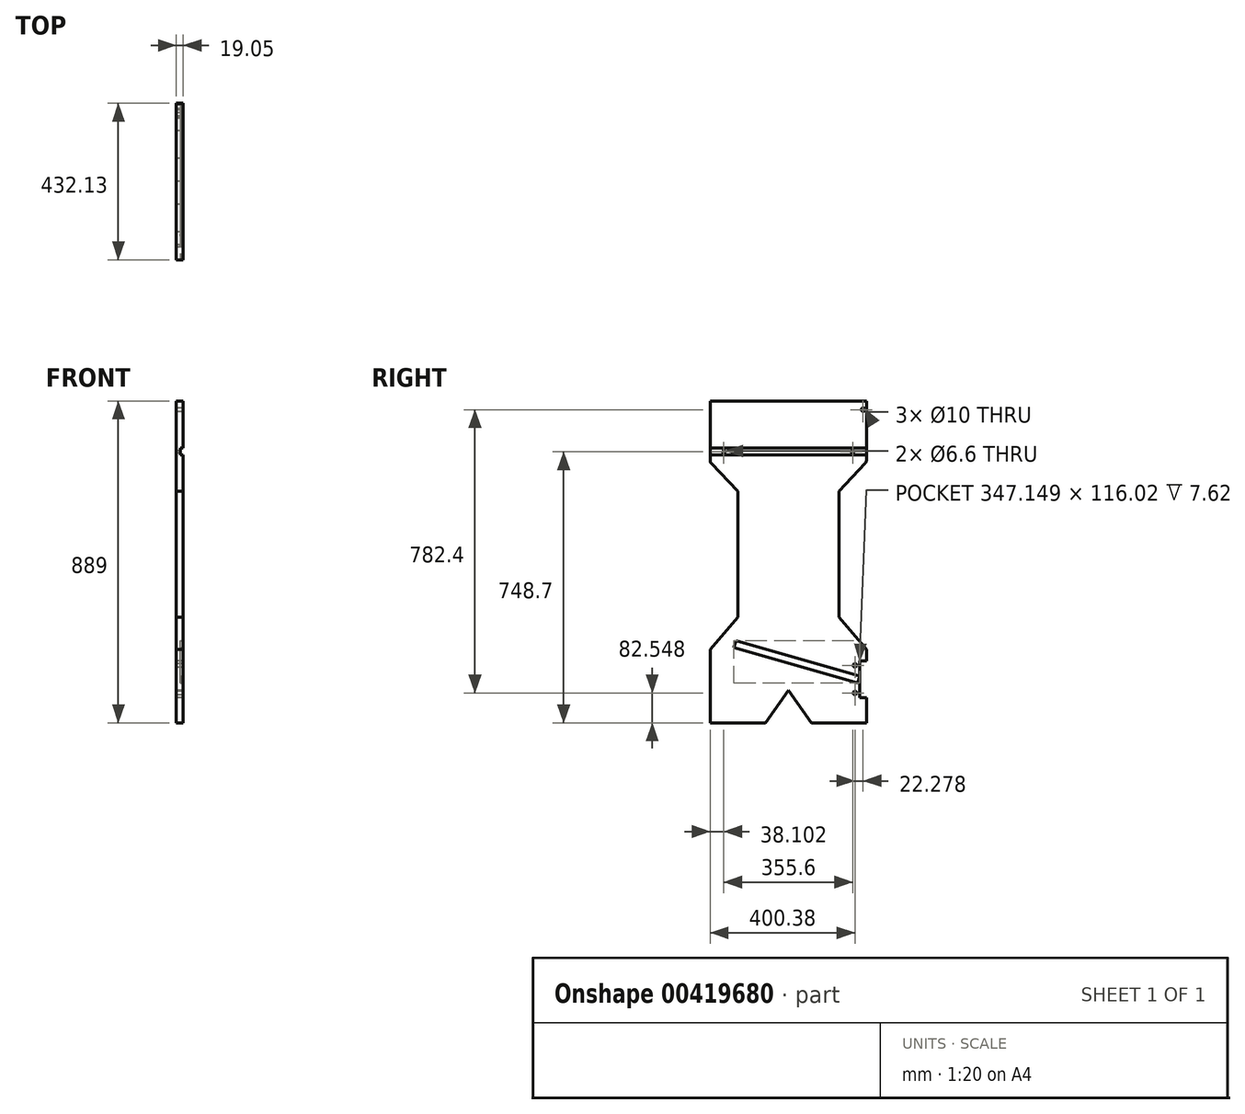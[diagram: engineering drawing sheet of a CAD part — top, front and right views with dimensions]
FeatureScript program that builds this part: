
annotation { "Feature Type Name" : "Feature", "Feature Type Description" : "" }
export const myFeature = defineFeature(function(context is Context, id is Id, definition is map)
    precondition{}
    {
        {
            var Q0;
            Q0=qCreatedBy(makeId("Right.planeOp"),FACE);
            var sketch = newSketch(context, id + "F0", { "sketchPlane" : qUnion([Q0])});
            skLineSegment(sketch, "E0.bottom", {"start": v(215.57, 77.66) * mm, "end": v(-216.23, 77.66) * mm});
            skLineSegment(sketch, "E0.left", {"start": v(215.57, 77.66) * mm, "end": v(215.57, -87.25) * mm});
            skLineSegment(sketch, "E0.right", {"start": v(-216.23, 77.66) * mm, "end": v(-216.23, -87.25) * mm});
            skPoint(sketch, "E0.middle", {"position": v(0, 0) * mm});
            skLineSegment(sketch, "E1", {"start": v(-213.4, -94.27) * mm, "end": v(-139.7, -171.26) * mm});
            skLineSegment(sketch, "E2", {"start": v(212.78, -94.24) * mm, "end": v(139.7, -171.26) * mm});
            skLineSegment(sketch, "E3", {"start": v(-139.7, -171.26) * mm, "end": v(-139.7, -519.24) * mm});
            skArc(sketch, "E4.filletArc", {"start": v(-216.23, -87.25) * mm, "mid": v(-215.5, -91.03) * mm, "end": v(-213.4, -94.27) * mm});
            skArc(sketch, "E5.filletArc", {"start": v(212.78, -94.24) * mm, "mid": v(214.85, -91.01) * mm, "end": v(215.57, -87.25) * mm});
            skLineSegment(sketch, "E6", {"start": v(-139.7, -519.24) * mm, "end": v(-215.9, -608.14) * mm});
            skLineSegment(sketch, "E7", {"start": v(-215.9, -608.14) * mm, "end": v(-215.9, -811.34) * mm});
            skLineSegment(sketch, "E8.MirrorCS", {"start": v(139.7, -171.26) * mm, "end": v(139.7, -519.24) * mm});
            skLineSegment(sketch, "E9.MirrorCS", {"start": v(139.7, -519.24) * mm, "end": v(215.9, -608.14) * mm});
            skLineSegment(sketch, "E10", {"start": v(-139.7, -171.26) * mm, "end": v(-42.85, -171.26) * mm, "construction": true});
            skLineSegment(sketch, "E11", {"start": v(-215.9, -608.14) * mm, "end": v(-139.7, -608.14) * mm, "construction": true});
            skLineSegment(sketch, "E12", {"start": v(-215.9, -811.34) * mm, "end": v(-63.5, -811.34) * mm});
            skLineSegment(sketch, "E13", {"start": v(-63.5, -811.34) * mm, "end": v(0, -721.49) * mm});
            skLineSegment(sketch, "E14", {"start": v(0, -721.49) * mm, "end": v(63.5, -811.34) * mm});
            skLineSegment(sketch, "E15", {"start": v(63.5, -811.34) * mm, "end": v(215.9, -811.34) * mm});
            skPoint(sketch, "E16", {"position": v(215.9, -639.9) * mm});
            skPoint(sketch, "E17", {"position": v(215.9, -741.5) * mm});
            skLineSegment(sketch, "E18", {"start": v(215.9, -639.9) * mm, "end": v(196.85, -639.9) * mm});
            skLineSegment(sketch, "E19", {"start": v(196.85, -639.9) * mm, "end": v(196.85, -741.5) * mm});
            skLineSegment(sketch, "E20", {"start": v(196.85, -741.5) * mm, "end": v(215.9, -741.5) * mm});
            skLineSegment(sketch, "E21", {"start": v(215.9, -608.14) * mm, "end": v(215.9, -639.9) * mm});
            skLineSegment(sketch, "E22", {"start": v(215.9, -741.5) * mm, "end": v(215.9, -811.34) * mm});
            skSolve(sketch);
        }
        {
            var Q0;
            Q0=qSketchRegion(id+"F0",true);
            extrude(context, id + "F1", {"entities" : qUnion([Q0]), "depth" : 19.05 * mm});
        }
        {
            var Q0;
            Q0=makeQuery(id+"F1.opExtrude","CAP_FACE",FACE,{"disambiguationData":[OSD([sQuery(id+"F0.wireOp",EDGE,"E0.bottom"),sQuery(id+"F0.wireOp",EDGE,"E0.left"),sQuery(id+"F0.wireOp",EDGE,"E0.right"),sQuery(id+"F0.wireOp",EDGE,"E1"),sQuery(id+"F0.wireOp",EDGE,"E2"),sQuery(id+"F0.wireOp",EDGE,"E3"),sQuery(id+"F0.wireOp",EDGE,"E4.filletArc"),sQuery(id+"F0.wireOp",EDGE,"E5.filletArc"),sQuery(id+"F0.wireOp",EDGE,"E6"),sQuery(id+"F0.wireOp",EDGE,"E7"),sQuery(id+"F0.wireOp",EDGE,"E8.MirrorCS"),sQuery(id+"F0.wireOp",EDGE,"E9.MirrorCS"),sQuery(id+"F0.wireOp",EDGE,"E12"),sQuery(id+"F0.wireOp",EDGE,"E13"),sQuery(id+"F0.wireOp",EDGE,"E14"),sQuery(id+"F0.wireOp",EDGE,"E15"),sQuery(id+"F0.wireOp",EDGE,"E18"),sQuery(id+"F0.wireOp",EDGE,"E19"),sQuery(id+"F0.wireOp",EDGE,"E20"),sQuery(id+"F0.wireOp",EDGE,"E21"),sQuery(id+"F0.wireOp",EDGE,"E22")])],"isStart":false});
            var sketch = newSketch(context, id + "F2", { "sketchPlane" : qUnion([Q0])});
            skLineSegment(sketch, "E23", {"start": v(196.84, -682.6) * mm, "end": v(191.6, -700.92) * mm});
            skLineSegment(sketch, "E24", {"start": v(191.6, -700.92) * mm, "end": v(-150.3, -603.22) * mm});
            skLineSegment(sketch, "E25", {"start": v(-150.3, -603.22) * mm, "end": v(-145.07, -584.9) * mm});
            skLineSegment(sketch, "E26", {"start": v(196.84, -682.6) * mm, "end": v(-145.07, -584.9) * mm});
            skSolve(sketch);
        }
        {
            var Q0;
            Q0=makeQuery(id+"F2.imprint","IMPRINT",FACE,{"disambiguationData":[TD([[makeQuery(id+"F2.imprint","IMPRINT",EDGE,{"derivedFrom":sQuery(id+"F2.wireOp",EDGE,"E23")}),-1.0]])]});
            extrude(context, id + "F3", {"entities" : qUnion([Q0]), "operationType" : NewBodyOperationType.REMOVE, "oppositeDirection" : true, "depth" : 7.62 * mm});
        }
        {
            var Q0;
            Q0=makeQuery(id+"F2.imprint","IMPRINT",FACE,{"disambiguationData":[TD([[makeQuery(id+"F2.imprint","IMPRINT",EDGE,{"derivedFrom":sQuery(id+"F2.wireOp",EDGE,"E23")}),1.0]])]});
            var sketch = newSketch(context, id + "F4", { "sketchPlane" : qUnion([Q0])});
            skLineSegment(sketch, "E27", {"start": v(216.17, -71.28) * mm, "end": v(-216.23, -71.28) * mm});
            skLineSegment(sketch, "E28", {"start": v(-216.23, -71.28) * mm, "end": v(-216.23, -52.23) * mm});
            skLineSegment(sketch, "E29", {"start": v(-216.23, -52.23) * mm, "end": v(215.57, -52.23) * mm});
            skLineSegment(sketch, "E30", {"start": v(215.57, -52.23) * mm, "end": v(216.17, -71.28) * mm});
            skSolve(sketch);
        }
        {
            var Q0;
            Q0=qSketchRegion(id+"F4",true);
            extrude(context, id + "F5", {"entities" : qUnion([Q0]), "operationType" : NewBodyOperationType.REMOVE, "oppositeDirection" : true, "depth" : 7.62 * mm});
        }
        {
            var Q0;
            Q0=makeQuery(id+"F0.imprint","IMPRINT",FACE,{"disambiguationData":[TD([[makeQuery(id+"F0.imprint","IMPRINT",EDGE,{"derivedFrom":sQuery(id+"F0.wireOp",EDGE,"E0.bottom")}),1.0]])]});
            var sketch = newSketch(context, id + "F6", { "sketchPlane" : qUnion([Q0])});
            skCircle(sketch, "E31", {"center": v(-178.13, -62.64) * mm, "radius": 3.3 * mm});
            skCircle(sketch, "E32", {"center": v(177.47, -62.64) * mm, "radius": 3.3 * mm});
            skCircle(sketch, "E33", {"center": v(206.43, 53.6) * mm, "radius": 5 * mm});
            skSolve(sketch);
        }
        {
            var Q0;
            Q0=qSketchRegion(id+"F6",true);
            extrude(context, id + "F7", {"entities" : qUnion([Q0]), "operationType" : NewBodyOperationType.REMOVE, "depth" : 19.05 * mm});
        }
        {
            var Q0;
            Q0=makeQuery(id+"F0.imprint","IMPRINT",FACE,{"disambiguationData":[TD([[makeQuery(id+"F0.imprint","IMPRINT",EDGE,{"derivedFrom":sQuery(id+"F0.wireOp",EDGE,"E0.bottom")}),1.0]])]});
            var sketch = newSketch(context, id + "F8", { "sketchPlane" : qUnion([Q0])});
            skPoint(sketch, "E34", {"position": v(196.85, -639.9) * mm});
            skPoint(sketch, "E35", {"position": v(196.85, -741.5) * mm});
            skLineSegment(sketch, "E36", {"start": v(196.85, -639.9) * mm, "end": v(184.15, -639.9) * mm, "construction": true});
            skLineSegment(sketch, "E37", {"start": v(184.15, -639.9) * mm, "end": v(184.15, -652.6) * mm, "construction": true});
            skLineSegment(sketch, "E38", {"start": v(196.85, -741.5) * mm, "end": v(184.15, -741.5) * mm, "construction": true});
            skLineSegment(sketch, "E39", {"start": v(184.15, -741.5) * mm, "end": v(184.15, -728.8) * mm, "construction": true});
            skCircle(sketch, "E40", {"center": v(184.15, -728.8) * mm, "radius": 5 * mm});
            skCircle(sketch, "E41", {"center": v(184.15, -652.6) * mm, "radius": 5 * mm});
            skSolve(sketch);
        }
        {
            var Q0;
            Q0=qSketchRegion(id+"F8",true);
            extrude(context, id + "F9", {"entities" : qUnion([Q0]), "operationType" : NewBodyOperationType.REMOVE, "depth" : 25.4 * mm, "offsetDistance" : 25.4 * mm});
        }
    });
